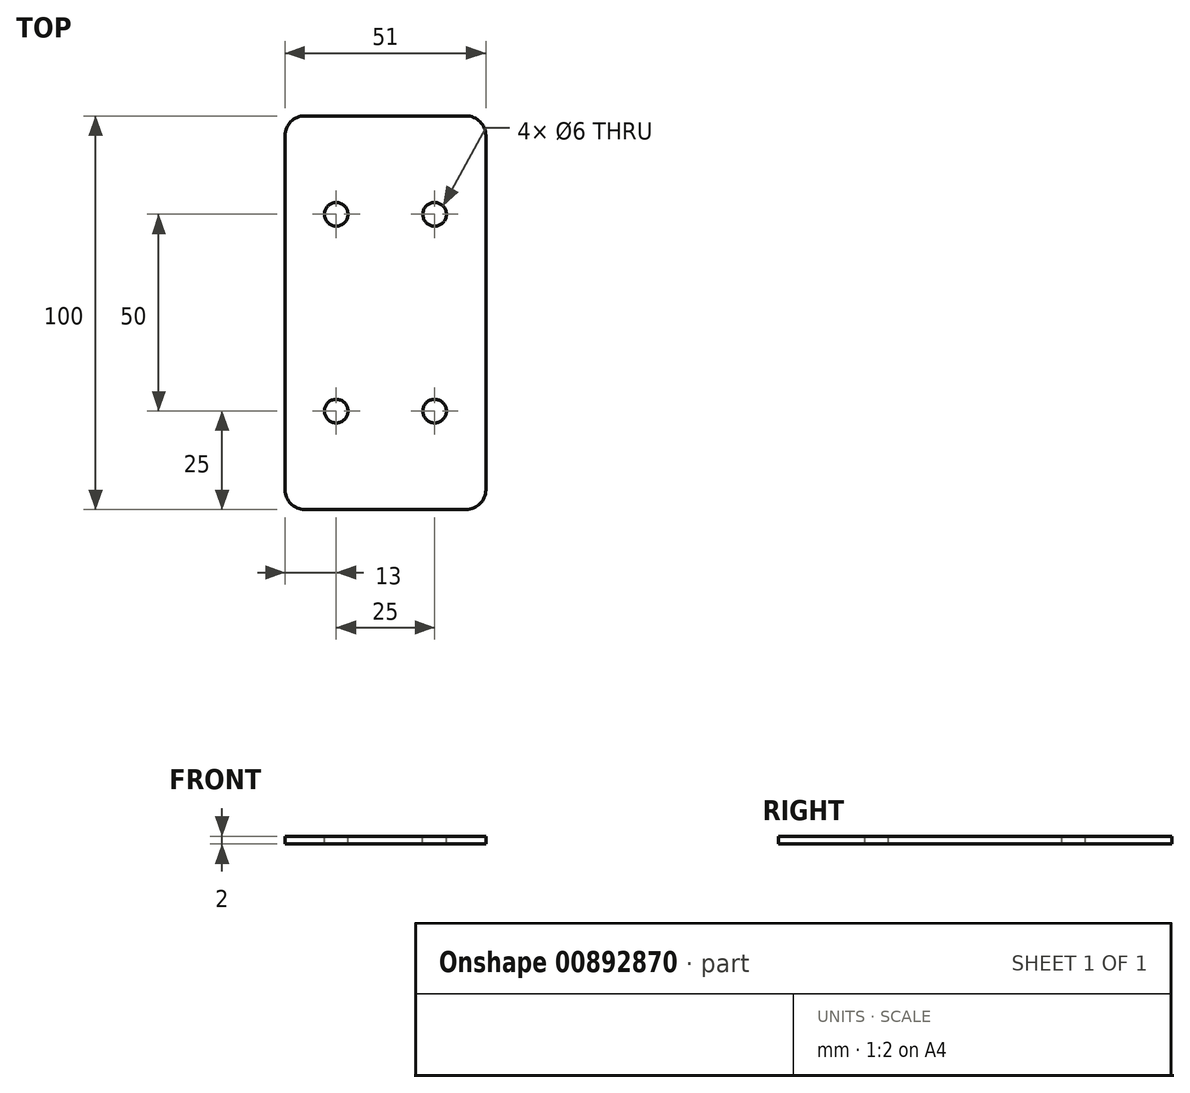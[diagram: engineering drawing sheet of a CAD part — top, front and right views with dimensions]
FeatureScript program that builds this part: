
annotation { "Feature Type Name" : "Feature", "Feature Type Description" : "" }
export const myFeature = defineFeature(function(context is Context, id is Id, definition is map)
    precondition{}
    {
        {
            var Q0;
            Q0=qCreatedBy(makeId("Top.planeOp"),FACE);
            var sketch = newSketch(context, id + "F0", { "sketchPlane" : qUnion([Q0])});
            skLineSegment(sketch, "E0.bottom", {"start": v(20.5, -50) * mm, "end": v(-20.5, -50) * mm});
            skLineSegment(sketch, "E0.top", {"start": v(20.5, 50) * mm, "end": v(-20.5, 50) * mm});
            skLineSegment(sketch, "E0.left", {"start": v(25.5, -45) * mm, "end": v(25.5, 45) * mm});
            skLineSegment(sketch, "E0.right", {"start": v(-25.5, -45) * mm, "end": v(-25.5, 45) * mm});
            skPoint(sketch, "E0.middle", {"position": v(0, 0) * mm});
            skPoint(sketch, "E1.visualSharp", {"position": v(-25.5, 50) * mm});
            skArc(sketch, "E1.filletArc", {"start": v(-20.5, 50) * mm, "mid": v(-24.04, 48.54) * mm, "end": v(-25.5, 45) * mm});
            skPoint(sketch, "E2.visualSharp", {"position": v(25.5, 50) * mm});
            skArc(sketch, "E2.filletArc", {"start": v(25.5, 45) * mm, "mid": v(24.04, 48.54) * mm, "end": v(20.5, 50) * mm});
            skPoint(sketch, "E3.visualSharp", {"position": v(25.5, -50) * mm});
            skArc(sketch, "E3.filletArc", {"start": v(20.5, -50) * mm, "mid": v(24.04, -48.54) * mm, "end": v(25.5, -45) * mm});
            skPoint(sketch, "E4.visualSharp", {"position": v(-25.5, -50) * mm});
            skArc(sketch, "E4.filletArc", {"start": v(-25.5, -45) * mm, "mid": v(-24.04, -48.54) * mm, "end": v(-20.5, -50) * mm});
            skSolve(sketch);
        }
        {
            var Q0;
            Q0 = qSketchRegion(id + "F0", true);
            extrude(context, id + "F1", {"entities" : qUnion([Q0]), "depth" : 2 * mm, "offsetDistance" : 25 * mm});
        }
        {
            var Q0;
            Q0=makeQuery(id+"F1.opExtrude","CAP_FACE",FACE,{"disambiguationData":[OSD([sQuery(id+"F0.wireOp",EDGE,"E0.bottom"),sQuery(id+"F0.wireOp",EDGE,"E0.top"),sQuery(id+"F0.wireOp",EDGE,"E0.left"),sQuery(id+"F0.wireOp",EDGE,"E0.right"),sQuery(id+"F0.wireOp",EDGE,"E1.filletArc"),sQuery(id+"F0.wireOp",EDGE,"E2.filletArc"),sQuery(id+"F0.wireOp",EDGE,"E3.filletArc"),sQuery(id+"F0.wireOp",EDGE,"E4.filletArc")])],"isStart":false});
            var sketch = newSketch(context, id + "F2", { "sketchPlane" : qUnion([Q0])});
            skLineSegment(sketch, "E5", {"start": v(-25.5, 0) * mm, "end": v(25.5, 0) * mm, "construction": true});
            skLineSegment(sketch, "E6", {"start": v(-25.5, -25) * mm, "end": v(25.5, -25) * mm, "construction": true});
            skLineSegment(sketch, "E7.MirrorCS", {"start": v(-25.5, 25) * mm, "end": v(25.5, 25) * mm, "construction": true});
            skLineSegment(sketch, "E8", {"start": v(0, 0) * mm, "end": v(0, 50) * mm, "construction": true});
            skCircle(sketch, "E9", {"center": v(-12.5, 25) * mm, "radius": 3 * mm});
            skCircle(sketch, "E10.MirrorC", {"center": v(12.5, 25) * mm, "radius": 3 * mm});
            skCircle(sketch, "E11.MirrorC", {"center": v(-12.5, -25) * mm, "radius": 3 * mm});
            skCircle(sketch, "E12.MirrorC", {"center": v(12.5, -25) * mm, "radius": 3 * mm});
            skSolve(sketch);
        }
        {
            var Q0;
            Q0 = qSketchRegion(id + "F2", true);
            extrude(context, id + "F3", {"entities" : qUnion([Q0]), "operationType" : NewBodyOperationType.REMOVE, "oppositeDirection" : true, "depth" : 25 * mm, "offsetDistance" : 25 * mm});
        }
    });
